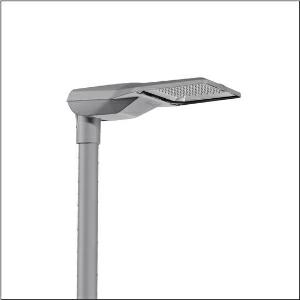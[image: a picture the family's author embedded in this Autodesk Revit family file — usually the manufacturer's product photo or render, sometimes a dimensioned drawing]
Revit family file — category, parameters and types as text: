
# Revit family: streetlight_sl_21_iq_midi___st0_8a_5xe3c41d08mb_0a8a
name_source: partatom
category: Lighting Fixtures
units: mm (PartAtom-declared; Revit-internal decimal feet)

## family parameters
Cut with Voids When Loaded = No
Host = Face
Light Source = No
Part Type = Normal
Room Calculation Point = No
Round Connector Dimension = Use Diameter
Shared = No

## types (1)
- --- (1 x LED, 20360 lm, 146.7 W, 4000K)
    Apparent Load = 147 VA
    CIE Flux Codes = 38 75 97 100 100
    Color Rendering = 70
    Color Temperature = 4000K
    Default Elevation = 1800 mm
    Description = Streetlight SL 21 iQ midi, mast luminaire, primary light control with lens, of PMMA, primary optical cover: cover, of toughened safety glass, transparent, light distribution: ST0.8a, light emission: direct distribution, primary light characteristic: asymmetric, installation type: post-top, side-entry, LED, High Power LED, rated luminous flux: 20.360lm, luminous efficacy: 139lm/W, light colour: 740, colour temperature: 4000K, control: Auto-Match, Temp-Guard, Lumen-Switch, Night-Set, Smart-Wire, Light-Fading, Desk-Remote (wireless, voltage-free reading and setting of iQ features in the workshop via application-optimized NFC function/RFID function), optimised constant luminous flux control (CLO 2.0), presetting dimming linear, mains connection: 230..240V, AC, 50/60Hz, start of lifetime: 147W, end of service life: 161W, reduction: 62W, luminaire housing, of diecast aluminium, powder-coated, Siteco® metallic grey (DB 702S), corrosivity category C5 mid according to DIN EN ISO 12944, please order mast flange separately, inclination adjustable: 0°, 5°, 10°, 15°, sealing non-destructively replaceable, multi-level sealing system, length: 644mm, width: 335mm, height: 110mm, mast flange for spigot size: 42mm (side-entry): 5XC10008XM4, 60/48mm (side-entry/post-top): 5XC10108XM2, 76/60mm (side-entry/post-top): 5XC10108XM1, protection rating (complete): IP66, insulation class (complete): insulation class II (safety insulation), certification: CE, ENEC, ENEC+, VDE, impact resistance: IK09, permissible operating ambient temperature for outdoor applications: -40..+50°C, standard-compliant lighting for roads and squares, packaging unit: 1 piece

Light Distribution: ST0.8a
    Height = 111 mm
    Lamp = 1 x LED
    Lamp Light Flux = 20360 lm
    Lamp Power = 146.7 W
    Lamp count = 1
    Length = 644 mm
    Luminous efficacy = 139 lm/W
    Manufacturer = Siteco
    ModVariant = No
    Model = 5XE3C41D08MB
    Number of Poles = 1
    OnlyDefault = Yes
    Power Factor = 1
    Product Name = Streetlight SL 21 iQ midi | ST0.8a
    Product group = mast luminaire | pylon top
    ProductGroupID = 6100
    Protection Class = Protection class II
    Protection Degree = IP 66
    RLX_Detail_Level = 1
    RLX_Emergency_Light_Flux = 0 lm
    RLX_Emergency_Type = 0
    RLX_Emergency_Type_DB = No
    RlxData = <blob elided: 90881 chars, md5=870b29fa>
    Socket = socket
    Standby Power = 0 W
    System Light Flux = 20360 lm
    System Power = 147 W
    Type Comments = factory setting: luminous flux: 100 % | dim-lin: 254 | 753 mA
    Type Image = l_1004298.jpg
    URL = http://relux.com
    VarID = @adj_119679
    Voltage = 0 V
    Weight = 0.00 kg
    Width = 336 mm

## geometry (parser evidence)
native form markers: Blend x4, Sweep x12
no freeform markers — native parametric forms only
